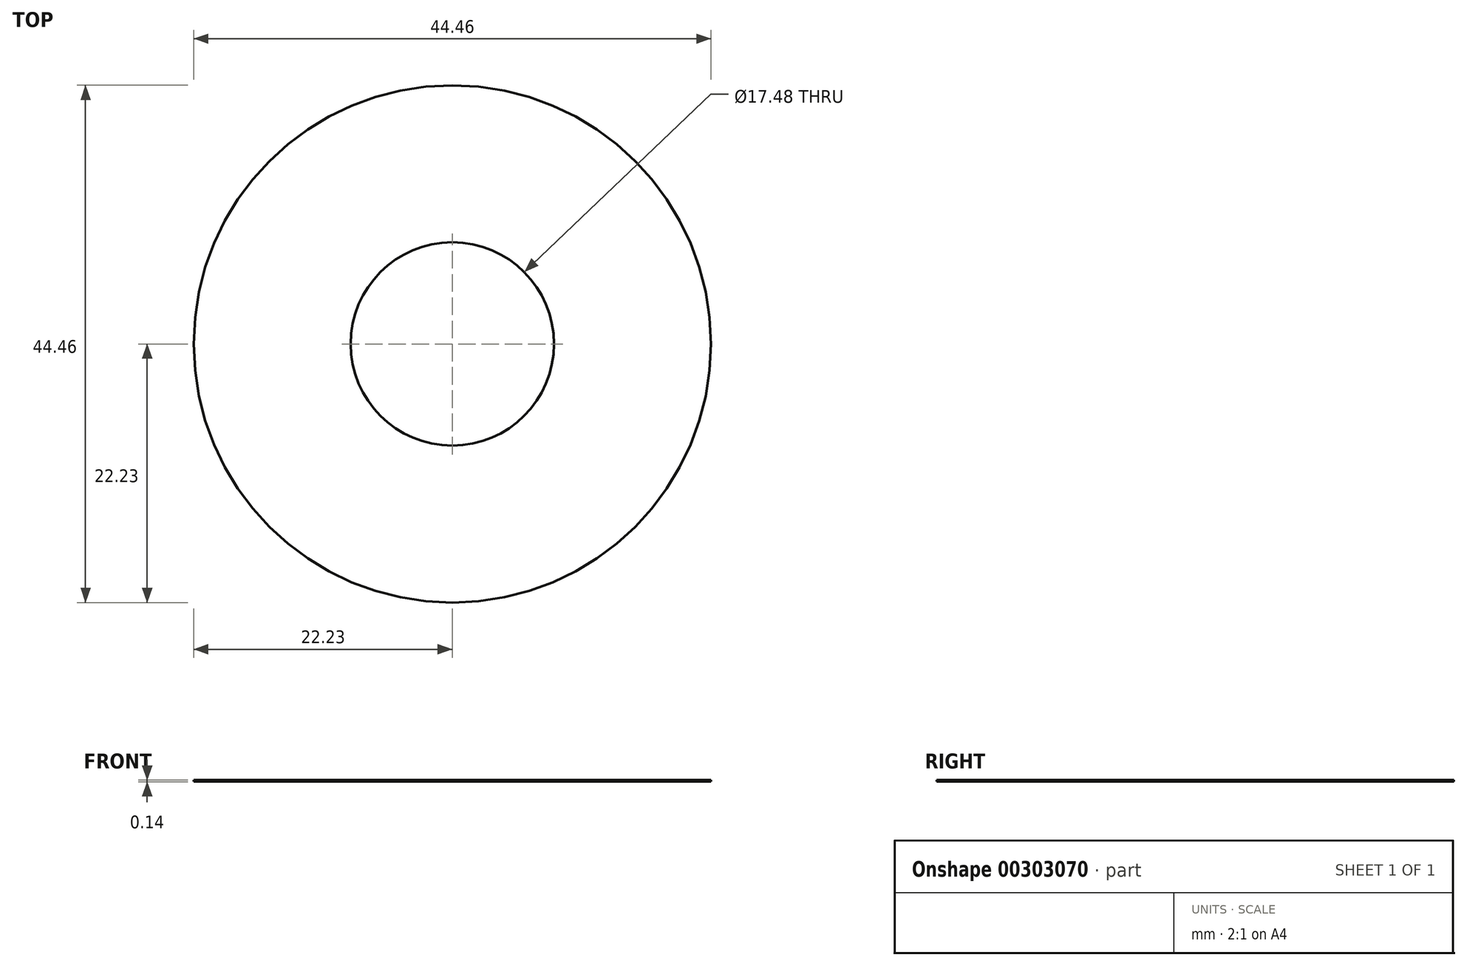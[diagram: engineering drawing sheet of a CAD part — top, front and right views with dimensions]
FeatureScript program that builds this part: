
annotation { "Feature Type Name" : "Feature", "Feature Type Description" : "" }
export const myFeature = defineFeature(function(context is Context, id is Id, definition is map)
    precondition{}
    {
        {
            var Q0;
            Q0=qCreatedBy(makeId("Top.planeOp"),FACE);
            var sketch = newSketch(context, id + "F0", { "sketchPlane" : qUnion([Q0])});
            skCircle(sketch, "E0", {"center": v(0, 0) * mm, "radius": 8.74 * mm});
            skCircle(sketch, "E1", {"center": v(0, 0) * mm, "radius": 22.23 * mm});
            skSolve(sketch);
        }
        {
            var Q0;
            Q0=makeQuery(id+"F0.imprint","IMPRINT",FACE,{"disambiguationData":[TD([[makeQuery(id+"F0.imprint","IMPRINT",EDGE,{"derivedFrom":sQuery(id+"F0.wireOp",EDGE,"E0")}),-1.0]])]});
            extrude(context, id + "F1", {"entities" : qUnion([Q0]), "depth" : ((0.1 + 0.16) / 2) * mm, "symmetric" : true});
        }
    });
